# Revit family: Reece_Toilet_Laufen_The New Classic_Pan Back to Wall_Rimless
name_source: partatom
category: Plumbing Fixtures
revit_build: Autodesk Revit 2018 (Build: 20190510_1515(x64)
units: mm (PartAtom-declared; Revit-internal decimal feet)

## family parameters
Always vertical = Yes
Cut with Voids When Loaded = Yes
Part Type = Normal
Room Calculation Point = No
Round Connector Dimension = Use Diameter
Shared = No
Work Plane-Based = Yes

## types (1)
- Soft Close _Vitreous China
    Default Elevation = 0 mm  [stored 0 ft]
    Description = LAUFEN New Classic Rimless Back to Wall Pan and Soft Close Quick Release Seat (4 Star)
    Disclaimer = THIS FILE IS THE PROPERTY OF THE REECE GROUP. IT MAY NOT BE REPRODUCED, REVERSE-ENGINEERED OR MODIFIED. ANY REPUBLICATION, TRANSMISSION OR DISTRIBUTION FOR THE PURPOSE OF COMMERCIALLY EXPLOITING THE FILES IS PROHIBITED.
    Keynote = Product #1813058, Reece_Toilet_Laufen_The New Classic_Pan Back to Wall_Rimless - Soft Close _Vitreous China
    Manufacturer = Laufen
    Model = The New Classic
    Reece_Back_Inlet = 55 mm  [stored 0.180446 ft]
    Reece_Back_Outlet_Offset = 185 mm  [stored 0.606955 ft]
    Reece_Bottom_Outlet_Offset = 95 mm  [stored 0.31168 ft]
    Reece_Detail_Additional = Pan Back to Wall
    Reece_Detail_Connector = Back Inlet
    Reece_Detail_Disclaimer = THIS FILE IS THE PROPERTY OF THE REECE GROUP. IT MAY NOT BE REPRODUCED, REVERSE-ENGINEERED OR MODIFIED. ANY REPUBLICATION, TRANSMISSION OR DISTRIBUTION FOR THE PURPOSE OF COMMERCIALLY EXPLOITING THE FILES IS PROHIBITED.
    Reece_Detail_Function = Universal S & P
    Reece_Detail_Shape = Rimless
    Reece_Material_Main = Reece_Vitreous China_White
    Reece_Material_Seat = Reece_Duroplast_White
    Reece_Material_Secondary = Reece_Brass_Chrome
    Reece_Overall_Height = 480 mm  [stored 1.5748 ft]
    Reece_Overall_Projection = 542 mm  [stored 1.77822 ft]
    Reece_Overall_Width = 395 mm  [stored 1.29593 ft]
    Reece_P_Trap = 102 mm
    Reece_Pan_Height = 430 mm  [stored 1.41076 ft]
    Reece_Pan_Projection = 530 mm  [stored 1.73885 ft]
    Reece_Pan_Width = 370 mm  [stored 1.21391 ft]
    Reece_Product_Brand = Laufen
    Reece_Product_Description = LAUFEN New Classic Rimless Back to Wall Pan and Soft Close Quick Release Seat (4 Star)
    Reece_Product_Mount = Floor Mounted
    Reece_Product_Number = 1813058
    Reece_Product_Sub Brand = The New Classic
    Reece_Product_Web Page = https://www.reece.com.au
    Reece_S_Trap = 106 mm  [stored 0.347769 ft]
    URL = https://www.reece.com.au

note: [stored X ft] marks values corroborated as IEEE doubles in the binary element streams (Revit-internal decimal feet)

## geometry (parser evidence)
native form markers: Sweep x7
no freeform markers — native parametric forms only
